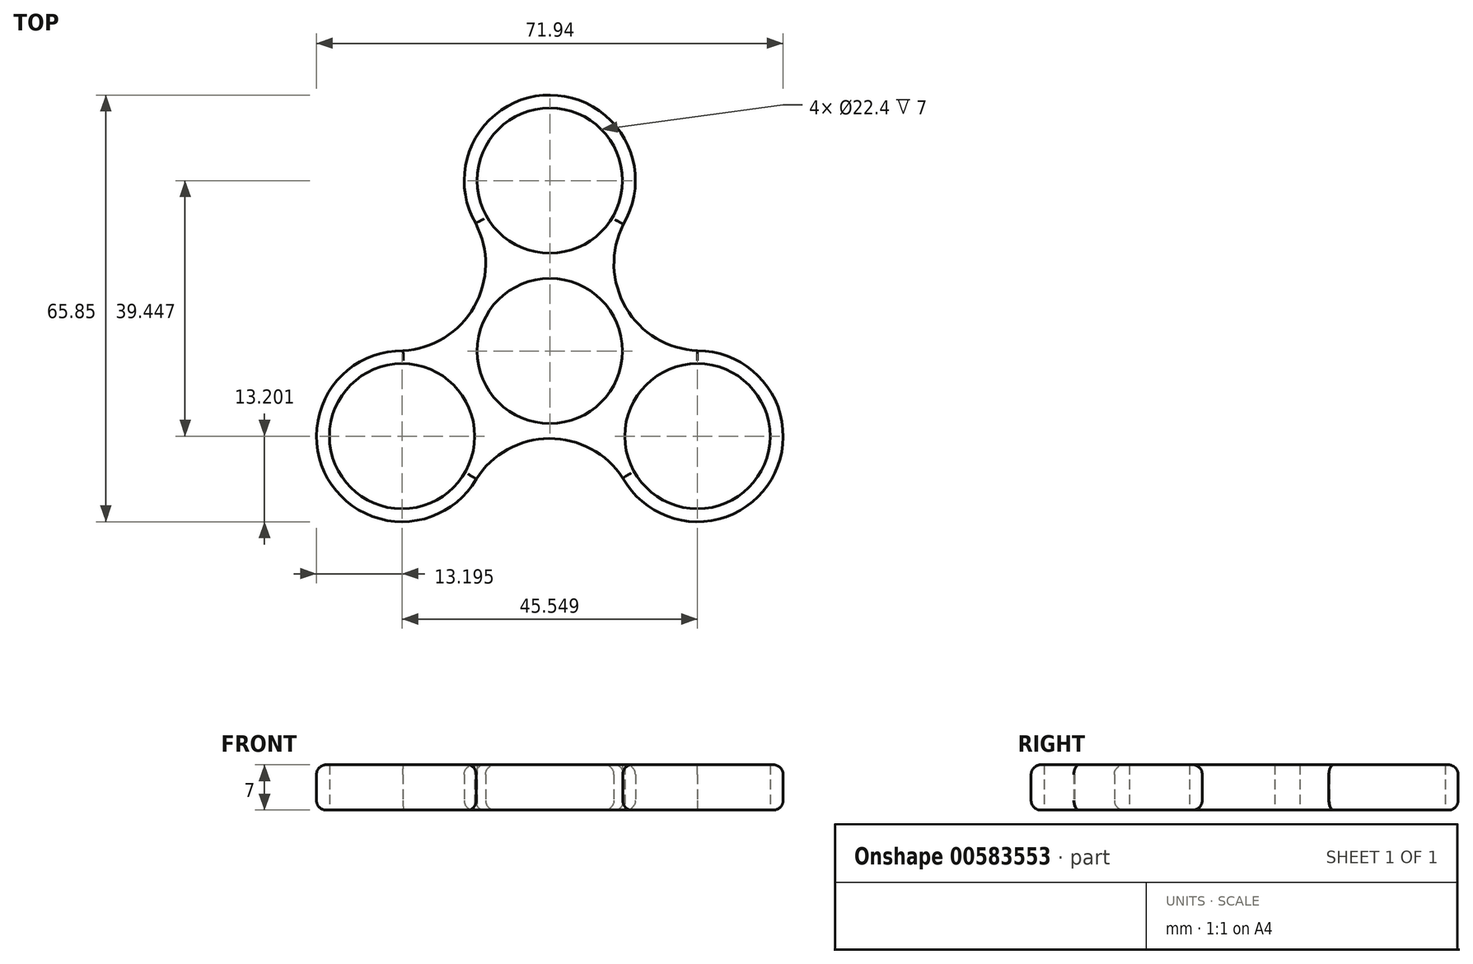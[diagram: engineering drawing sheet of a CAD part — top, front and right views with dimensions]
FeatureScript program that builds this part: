
annotation { "Feature Type Name" : "Feature", "Feature Type Description" : "" }
export const myFeature = defineFeature(function(context is Context, id is Id, definition is map)
    precondition{}
    {
        {
            var Q0;
            Q0=qCreatedBy(makeId("Top.planeOp"),FACE);
            var sketch = newSketch(context, id + "F0", { "sketchPlane" : qUnion([Q0])});
            skCircle(sketch, "E0", {"center": v(0, 0) * mm, "radius": 11.2 * mm});
            skCircle(sketch, "E1", {"center": v(0, 26.3) * mm, "radius": 11.2 * mm});
            skArc(sketch, "E2", {"start": v(11.35, 19.56) * mm, "mid": v(0.08, 39.5) * mm, "end": v(-11.43, 19.7) * mm});
            skArc(sketch, "E3.1.0", {"start": v(-22.62, 0.05) * mm, "mid": v(-34.25, -19.68) * mm, "end": v(-11.34, -19.75) * mm});
            skCircle(sketch, "E3.1.1", {"center": v(-22.77, -13.15) * mm, "radius": 11.2 * mm});
            skCircle(sketch, "E3.2.1", {"center": v(22.77, -13.15) * mm, "radius": 11.2 * mm});
            skArc(sketch, "E4", {"start": v(11.35, 19.56) * mm, "mid": v(11.73, 6.69) * mm, "end": v(22.77, 0.05) * mm});
            skArc(sketch, "E5.1.0", {"start": v(-22.62, 0.05) * mm, "mid": v(-11.66, 6.82) * mm, "end": v(-11.43, 19.7) * mm});
            skArc(sketch, "E5.2.0", {"start": v(11.27, -19.61) * mm, "mid": v(-0.08, -13.5) * mm, "end": v(-11.34, -19.75) * mm});
            skLineSegment(sketch, "E6.trimOffspring", {"start": v(10.87, 7.5) * mm, "end": v(11.2, 7.7) * mm, "construction": true});
            skPoint(sketch, "E7.orphan", {"position": v(22.77, 14.8) * mm});
            skArc(sketch, "E8.trimOffspring", {"start": v(10.87, 7.5) * mm, "mid": v(10.84, 7.54) * mm, "end": v(10.8, 7.58) * mm});
            skArc(sketch, "E9.trimOffspring", {"start": v(11.27, -19.61) * mm, "mid": v(34.17, -19.82) * mm, "end": v(22.77, 0.05) * mm});
            skLineSegment(sketch, "E10.trimOffspring", {"start": v(10.8, 7.58) * mm, "end": v(10.86, 7.49) * mm, "construction": true});
            skSolve(sketch);
        }
        {
            var Q0;
            Q0=makeQuery(id+"F0.imprint","IMPRINT",FACE,{"disambiguationData":[TD([[makeQuery(id+"F0.imprint","IMPRINT",EDGE,{"derivedFrom":sQuery(id+"F0.wireOp",EDGE,"E0")}),-1.0]])]});
            extrude(context, id + "F1", {"entities" : qUnion([Q0]), "depth" : 7 * mm, "offsetDistance" : 25 * mm});
        }
        {
            var Q0;
            Q0=makeQuery(id+"F1.opExtrude","CAP_EDGE",EDGE,{"disambiguationData":[OSD([sQuery(id+"F0.wireOp",EDGE,"E5.2.0")])],"isStart":false});
            var Q1;
            Q1=makeQuery(id+"F1.opExtrude","CAP_EDGE",EDGE,{"disambiguationData":[OSD([sQuery(id+"F0.wireOp",EDGE,"E3.1.0")])],"isStart":false});
            var Q2;
            Q2=makeQuery(id+"F1.opExtrude","CAP_EDGE",EDGE,{"disambiguationData":[OSD([sQuery(id+"F0.wireOp",EDGE,"E5.1.0")])],"isStart":false});
            var Q3;
            Q3=makeQuery(id+"F1.opExtrude","CAP_EDGE",EDGE,{"disambiguationData":[OSD([sQuery(id+"F0.wireOp",EDGE,"E2")])],"isStart":false});
            var Q4;
            Q4=makeQuery(id+"F1.opExtrude","CAP_EDGE",EDGE,{"disambiguationData":[OSD([sQuery(id+"F0.wireOp",EDGE,"E4")])],"isStart":false});
            var Q5;
            Q5=makeQuery(id+"F1.opExtrude","CAP_EDGE",EDGE,{"disambiguationData":[OSD([sQuery(id+"F0.wireOp",EDGE,"E9.trimOffspring")])],"isStart":false});
            fillet(context, id + "F2", {"entities" : qUnion([Q0, Q1, Q2, Q3, Q4, Q5]), "radius" : 1.5 * mm, "tangentPropagation" : true, "allowEdgeOverflow" : false});
        }
        {
            var Q0;
            Q0=makeQuery(id+"F1.opExtrude","CAP_EDGE",EDGE,{"disambiguationData":[OSD([sQuery(id+"F0.wireOp",EDGE,"E5.2.0")])],"isStart":true});
            var Q1;
            Q1=makeQuery(id+"F1.opExtrude","CAP_EDGE",EDGE,{"disambiguationData":[OSD([sQuery(id+"F0.wireOp",EDGE,"E3.1.0")])],"isStart":true});
            var Q2;
            Q2=makeQuery(id+"F1.opExtrude","CAP_EDGE",EDGE,{"disambiguationData":[OSD([sQuery(id+"F0.wireOp",EDGE,"E5.1.0")])],"isStart":true});
            var Q3;
            Q3=makeQuery(id+"F1.opExtrude","CAP_EDGE",EDGE,{"disambiguationData":[OSD([sQuery(id+"F0.wireOp",EDGE,"E2")])],"isStart":true});
            var Q4;
            Q4=makeQuery(id+"F1.opExtrude","CAP_EDGE",EDGE,{"disambiguationData":[OSD([sQuery(id+"F0.wireOp",EDGE,"E4")])],"isStart":true});
            var Q5;
            Q5=makeQuery(id+"F1.opExtrude","CAP_EDGE",EDGE,{"disambiguationData":[OSD([sQuery(id+"F0.wireOp",EDGE,"E9.trimOffspring")])],"isStart":true});
            fillet(context, id + "F3", {"entities" : qUnion([Q0, Q1, Q2, Q3, Q4, Q5]), "radius" : 1.5 * mm, "tangentPropagation" : true, "allowEdgeOverflow" : false});
        }
    });
